# Revit family: ABW-R1X08525xx
name_source: partatom
category: Leuchten
units: mm (PartAtom-declared; Revit-internal decimal feet)

## family parameters
Basisbauteil = Fläche
Beim Laden mit Abzugskörper schneiden = Nein
Bemaßung runder Anschluss = Durchmesser verwenden
Gemeinsam genutzt = Nein
Lichtquelle = Ja
OmniClass-Nummer = 23.80.70.11
OmniClass-Titel = Luminaries for Internal Lighting
Raumberechnungspunkt = Nein
Teiletyp = Normal

## types (2) — shared parameters
Baugruppenkennzeichen = D5020200
Datei für fotometrisches Netz = ABW-R1.IES
Emissionsform beim Rendern sichtbar = Nein
Farbfilter = 16777215
Farbtemperaturverschiebung bei Dämpfen der Lampe = <Keine Auswahl>
Hersteller = RIDI Leuchten GmbH
Lampe = LED
Neigungswinkel = 90.00°
Scheinlast = 22 VA
URL = www.ridi.de
Von Breite des Rechtecks ausssenden = 898 mm  [stored 2.94619 ft]
Von Länge des Rechtecks aussenden = 132 mm  [stored 0.433071 ft]
brand = RIDI
conformity mark = CE
electrical safety class = 1
height = 72 mm  [stored 0.23622 ft]
ingress protection (IP) code = IP20
length = 900 mm  [stored 2.95276 ft]
nominal frequency = 50-60Hz
nominal voltage = 230
rated input power = 22
voltage type (AC, DC, UC) = AC
weight = 3,492
width = 193 mm  [stored 0.633202 ft]
zero-valued in all types: Vorgabe-Ansicht

## per-type parameters (varying)
| type | Modell |
| ABW-R1X085/25ND | 0650347 |
| ABW-R1X085/25DA | 0660347 |

note: column(s) folded — value = type name in every type: product name

note: [stored X ft] marks values corroborated as IEEE doubles in the binary element streams (Revit-internal decimal feet)
